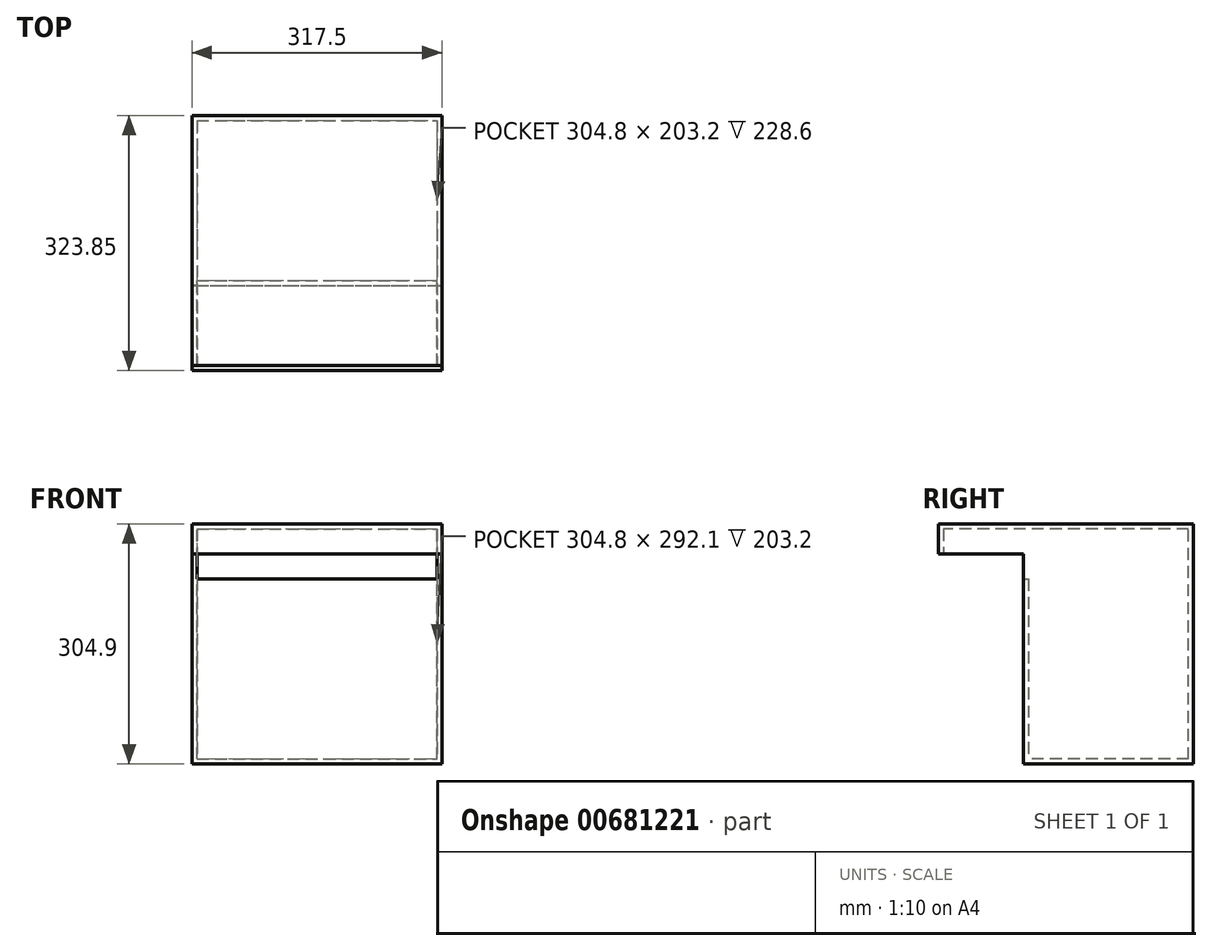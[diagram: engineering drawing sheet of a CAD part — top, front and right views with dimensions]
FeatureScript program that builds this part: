
annotation { "Feature Type Name" : "Feature", "Feature Type Description" : "" }
export const myFeature = defineFeature(function(context is Context, id is Id, definition is map)
    precondition{}
    {
        {
            var Q0;
            Q0=qCreatedBy(makeId("Top.planeOp"),FACE);
            var sketch = newSketch(context, id + "F0", { "sketchPlane" : qUnion([Q0])});
            skLineSegment(sketch, "E0.bottom", {"start": v(0, 0) * mm, "end": v(317.5, 0) * mm});
            skLineSegment(sketch, "E0.top", {"start": v(0, -215.9) * mm, "end": v(317.5, -215.9) * mm});
            skLineSegment(sketch, "E0.left", {"start": v(0, 0) * mm, "end": v(0, -215.9) * mm});
            skLineSegment(sketch, "E0.right", {"start": v(317.5, 0) * mm, "end": v(317.5, -215.9) * mm});
            skSolve(sketch);
        }
        {
            var Q0;
            Q0 = qSketchRegion(id + "F0", true);
            extrude(context, id + "F1", {"entities" : qUnion([Q0]), "oppositeDirection" : true, "depth" : 6.35 * mm, "offsetDistance" : 25.4 * mm});
        }
        {
            var Q0;
            Q0=qCreatedBy(makeId("Front.planeOp"),FACE);
            var sketch = newSketch(context, id + "F2", { "sketchPlane" : qUnion([Q0])});
            skLineSegment(sketch, "E1.bottom", {"start": v(0, 0) * mm, "end": v(317.5, 0) * mm});
            skLineSegment(sketch, "E1.top", {"start": v(0, 292.1) * mm, "end": v(317.5, 292.1) * mm});
            skLineSegment(sketch, "E1.left", {"start": v(0, 0) * mm, "end": v(0, 292.1) * mm});
            skLineSegment(sketch, "E1.right", {"start": v(317.5, 0) * mm, "end": v(317.5, 292.1) * mm});
            skSolve(sketch);
        }
        {
            var Q0;
            Q0=makeQuery(id+"F2.imprint","IMPRINT",FACE,{"disambiguationData":[TD([[makeQuery(id+"F2.imprint","IMPRINT",EDGE,{"derivedFrom":sQuery(id+"F2.wireOp",EDGE,"E1.bottom")}),1.0]])]});
            extrude(context, id + "F3", {"entities" : qUnion([Q0]), "operationType" : NewBodyOperationType.ADD, "depth" : 6.35 * mm, "offsetDistance" : 25.4 * mm});
        }
        {
            var Q0;
            Q0=qCreatedBy(makeId("Right.planeOp"),FACE);
            var sketch = newSketch(context, id + "F4", { "sketchPlane" : qUnion([Q0])});
            skLineSegment(sketch, "E2.bottom", {"start": v(0, 0) * mm, "end": v(-215.9, 0) * mm});
            skLineSegment(sketch, "E2.top", {"start": v(0, 292.1) * mm, "end": v(-215.9, 292.1) * mm});
            skLineSegment(sketch, "E2.left", {"start": v(0, 0) * mm, "end": v(0, 292.1) * mm});
            skLineSegment(sketch, "E2.right", {"start": v(-215.9, 0) * mm, "end": v(-215.9, 292.1) * mm});
            skSolve(sketch);
        }
        {
            var Q0;
            Q0=makeQuery(id+"F4.imprint","IMPRINT",FACE,{"disambiguationData":[TD([[makeQuery(id+"F4.imprint","IMPRINT",EDGE,{"derivedFrom":sQuery(id+"F4.wireOp",EDGE,"E2.bottom")}),-1.0]])]});
            extrude(context, id + "F5", {"entities" : qUnion([Q0]), "operationType" : NewBodyOperationType.ADD, "depth" : 6.35 * mm, "offsetDistance" : 25.4 * mm});
        }
        {
            var Q0;
            Q0=makeQuery(id+"F3.boolean.opBoolean","MERGE",FACE,{"derivedFrom":[makeQuery(id+"F1.opExtrude","SWEPT_FACE",FACE,{"disambiguationData":[OSD([sQuery(id+"F0.wireOp",EDGE,"E0.right")])]}),makeQuery(id+"F3.opExtrude","SWEPT_FACE",FACE,{"disambiguationData":[OSD([sQuery(id+"F2.wireOp",EDGE,"E1.right")])]})]});
            cPlane(context, id + "F6", {"entities" : qUnion([Q0]), "cplaneType" : CPlaneType.OFFSET, "offset" : 0 * mm, "width" : 152.4 * mm, "height" : 152.4 * mm});
        }
        {
            var Q0;
            Q0=qCreatedBy(id+"F6.planeOp",FACE);
            var sketch = newSketch(context, id + "F7", { "sketchPlane" : qUnion([Q0])});
            skLineSegment(sketch, "E3.bottom", {"start": v(0, 292.1) * mm, "end": v(-215.9, 292.1) * mm});
            skLineSegment(sketch, "E3.top", {"start": v(0, 0) * mm, "end": v(-215.9, 0) * mm});
            skLineSegment(sketch, "E3.left", {"start": v(0, 292.1) * mm, "end": v(0, 0) * mm});
            skLineSegment(sketch, "E3.right", {"start": v(-215.9, 292.1) * mm, "end": v(-215.9, 0) * mm});
            skSolve(sketch);
        }
        {
            var Q0;
            Q0 = qSketchRegion(id + "F7", true);
            extrude(context, id + "F8", {"entities" : qUnion([Q0]), "operationType" : NewBodyOperationType.ADD, "oppositeDirection" : true, "depth" : 6.35 * mm, "offsetDistance" : 25.4 * mm});
        }
        {
            var Q0;
            Q0=makeQuery(id+"F8.boolean.opBoolean","MERGE",FACE,{"derivedFrom":[makeQuery(id+"F5.boolean.opBoolean","MERGE",FACE,{"derivedFrom":[makeQuery(id+"F3.opExtrude","SWEPT_FACE",FACE,{"disambiguationData":[OSD([sQuery(id+"F2.wireOp",EDGE,"E1.top")])]}),makeQuery(id+"F5.opExtrude","SWEPT_FACE",FACE,{"disambiguationData":[OSD([sQuery(id+"F4.wireOp",EDGE,"E2.top")])]})]}),makeQuery(id+"F8.opExtrude","SWEPT_FACE",FACE,{"disambiguationData":[OSD([sQuery(id+"F7.wireOp",EDGE,"E3.bottom")])]})]});
            cPlane(context, id + "F9", {"entities" : qUnion([Q0]), "cplaneType" : CPlaneType.OFFSET, "offset" : 0 * mm, "width" : 152.4 * mm, "height" : 152.4 * mm});
        }
        {
            var Q0;
            Q0=qCreatedBy(id+"F9.planeOp",FACE);
            var sketch = newSketch(context, id + "F10", { "sketchPlane" : qUnion([Q0])});
            skLineSegment(sketch, "E4.bottom", {"start": v(0, 0) * mm, "end": v(317.5, 0) * mm});
            skLineSegment(sketch, "E4.top", {"start": v(0, -317.5) * mm, "end": v(317.5, -317.5) * mm});
            skLineSegment(sketch, "E4.left", {"start": v(0, 0) * mm, "end": v(0, -317.5) * mm});
            skLineSegment(sketch, "E4.right", {"start": v(317.5, 0) * mm, "end": v(317.5, -317.5) * mm});
            skSolve(sketch);
        }
        {
            var Q0;
            Q0=makeQuery(id+"F10.imprint","IMPRINT",FACE,{"disambiguationData":[TD([[makeQuery(id+"F10.imprint","IMPRINT",EDGE,{"derivedFrom":sQuery(id+"F10.wireOp",EDGE,"E4.bottom")}),-1.0]])]});
            extrude(context, id + "F11", {"entities" : qUnion([Q0]), "operationType" : NewBodyOperationType.ADD, "depth" : 6.35 * mm, "offsetDistance" : 25.4 * mm});
        }
        {
            var Q0;
            Q0=makeQuery(id+"F11.opExtrude","SWEPT_FACE",FACE,{"disambiguationData":[OSD([sQuery(id+"F10.wireOp",EDGE,"E4.top")])]});
            cPlane(context, id + "F12", {"entities" : qUnion([Q0]), "cplaneType" : CPlaneType.OFFSET, "offset" : 0 * mm, "width" : 152.4 * mm, "height" : 152.4 * mm});
        }
        {
            var Q0;
            Q0=makeQuery(id+"F8.boolean.opBoolean","MERGE",FACE,{"derivedFrom":[makeQuery(id+"F5.boolean.opBoolean","MERGE",FACE,{"derivedFrom":[makeQuery(id+"F1.opExtrude","SWEPT_FACE",FACE,{"disambiguationData":[OSD([sQuery(id+"F0.wireOp",EDGE,"E0.top")])]}),makeQuery(id+"F5.opExtrude","SWEPT_FACE",FACE,{"disambiguationData":[OSD([sQuery(id+"F4.wireOp",EDGE,"E2.right")])]})]}),makeQuery(id+"F8.opExtrude","SWEPT_FACE",FACE,{"disambiguationData":[OSD([sQuery(id+"F7.wireOp",EDGE,"E3.right")])]})]});
            cPlane(context, id + "F13", {"entities" : qUnion([Q0]), "cplaneType" : CPlaneType.OFFSET, "offset" : 0 * mm, "oppositeDirection" : true, "width" : 152.4 * mm, "height" : 152.4 * mm});
        }
        {
            var Q0;
            Q0=qCreatedBy(id+"F13.planeOp",FACE);
            var sketch = newSketch(context, id + "F14", { "sketchPlane" : qUnion([Q0])});
            skLineSegment(sketch, "E5.bottom", {"start": v(0, 228.6) * mm, "end": v(317.5, 228.6) * mm});
            skLineSegment(sketch, "E5.top", {"start": v(0, 0) * mm, "end": v(317.5, 0) * mm});
            skLineSegment(sketch, "E5.left", {"start": v(0, 228.6) * mm, "end": v(0, 0) * mm});
            skLineSegment(sketch, "E5.right", {"start": v(317.5, 228.6) * mm, "end": v(317.5, 0) * mm});
            skSolve(sketch);
        }
        {
            var Q0;
            Q0 = qSketchRegion(id + "F14", true);
            extrude(context, id + "F15", {"entities" : qUnion([Q0]), "operationType" : NewBodyOperationType.ADD, "oppositeDirection" : true, "depth" : 6.35 * mm, "offsetDistance" : 25.4 * mm});
        }
        {
            var Q0;
            Q0=makeQuery(id+"FhI14EcKR7AobF6_1.boolean.opBoolean","MERGE",FACE,{"derivedFrom":[makeQuery(id+"F11.boolean.opBoolean","MERGE",FACE,{"derivedFrom":[makeQuery(id+"F8.boolean.opBoolean","MERGE",FACE,{"derivedFrom":[makeQuery(id+"F3.boolean.opBoolean","MERGE",FACE,{"derivedFrom":[makeQuery(id+"F1.opExtrude","SWEPT_FACE",FACE,{"disambiguationData":[OSD([sQuery(id+"F0.wireOp",EDGE,"E0.right")])]}),makeQuery(id+"F3.opExtrude","SWEPT_FACE",FACE,{"disambiguationData":[OSD([sQuery(id+"F2.wireOp",EDGE,"E1.right")])]})]}),makeQuery(id+"F8.opExtrude","CAP_FACE",FACE,{"disambiguationData":[OSD([sQuery(id+"F7.wireOp",EDGE,"E3.bottom"),sQuery(id+"F7.wireOp",EDGE,"E3.top"),sQuery(id+"F7.wireOp",EDGE,"E3.left"),sQuery(id+"F7.wireOp",EDGE,"E3.right")])],"isStart":true})]}),makeQuery(id+"F11.opExtrude","SWEPT_FACE",FACE,{"disambiguationData":[OSD([sQuery(id+"F10.wireOp",EDGE,"E4.right")])]})]}),makeQuery(id+"FhI14EcKR7AobF6_1.opExtrude","SWEPT_FACE",FACE,{"disambiguationData":[OSD([sQuery(id+"FLD8qPjJOVZHiva_1.wireOp",EDGE,"Go6pk4AO-W8t4-oNwY-yMQV-z4UT52Fjz0Ug.right")])]})]});
            var sketch = newSketch(context, id + "F16", { "sketchPlane" : qUnion([Q0])});
            skLineSegment(sketch, "E6.bottom", {"start": v(-317.5, 298.45) * mm, "end": v(-215.9, 298.45) * mm});
            skLineSegment(sketch, "E6.top", {"start": v(-317.5, 260.35) * mm, "end": v(-215.9, 260.35) * mm});
            skLineSegment(sketch, "E6.left", {"start": v(-317.5, 298.45) * mm, "end": v(-317.5, 260.35) * mm});
            skLineSegment(sketch, "E6.right", {"start": v(-215.9, 298.45) * mm, "end": v(-215.9, 260.35) * mm});
            skSolve(sketch);
        }
        {
            var Q0;
            Q0 = qSketchRegion(id + "F16", true);
            extrude(context, id + "F17", {"entities" : qUnion([Q0]), "operationType" : NewBodyOperationType.ADD, "oppositeDirection" : true, "depth" : 6.35 * mm, "offsetDistance" : 25.4 * mm});
        }
        {
            var Q0;
            Q0=makeQuery(id+"FhI14EcKR7AobF6_1.boolean.opBoolean","MERGE",FACE,{"derivedFrom":[makeQuery(id+"F11.boolean.opBoolean","MERGE",FACE,{"derivedFrom":[makeQuery(id+"F5.boolean.opBoolean","MERGE",FACE,{"derivedFrom":[makeQuery(id+"F3.boolean.opBoolean","MERGE",FACE,{"derivedFrom":[makeQuery(id+"F1.opExtrude","SWEPT_FACE",FACE,{"disambiguationData":[OSD([sQuery(id+"F0.wireOp",EDGE,"E0.left")])]}),makeQuery(id+"F3.opExtrude","SWEPT_FACE",FACE,{"disambiguationData":[OSD([sQuery(id+"F2.wireOp",EDGE,"E1.left")])]})]}),makeQuery(id+"F5.opExtrude","CAP_FACE",FACE,{"disambiguationData":[OSD([sQuery(id+"F4.wireOp",EDGE,"E2.bottom"),sQuery(id+"F4.wireOp",EDGE,"E2.top"),sQuery(id+"F4.wireOp",EDGE,"E2.left"),sQuery(id+"F4.wireOp",EDGE,"E2.right")])],"isStart":true})]}),makeQuery(id+"F11.opExtrude","SWEPT_FACE",FACE,{"disambiguationData":[OSD([sQuery(id+"F10.wireOp",EDGE,"E4.left")])]})]}),makeQuery(id+"FhI14EcKR7AobF6_1.opExtrude","SWEPT_FACE",FACE,{"disambiguationData":[OSD([sQuery(id+"FLD8qPjJOVZHiva_1.wireOp",EDGE,"Go6pk4AO-W8t4-oNwY-yMQV-z4UT52Fjz0Ug.left")])]})]});
            var sketch = newSketch(context, id + "F18", { "sketchPlane" : qUnion([Q0])});
            skLineSegment(sketch, "E7.bottom", {"start": v(317.5, 298.45) * mm, "end": v(215.9, 298.45) * mm});
            skLineSegment(sketch, "E7.top", {"start": v(317.5, 260.35) * mm, "end": v(215.9, 260.35) * mm});
            skLineSegment(sketch, "E7.left", {"start": v(317.5, 298.45) * mm, "end": v(317.5, 260.35) * mm});
            skLineSegment(sketch, "E7.right", {"start": v(215.9, 298.45) * mm, "end": v(215.9, 260.35) * mm});
            skSolve(sketch);
        }
        {
            var Q0;
            Q0 = qSketchRegion(id + "F18", true);
            extrude(context, id + "F19", {"entities" : qUnion([Q0]), "operationType" : NewBodyOperationType.ADD, "oppositeDirection" : true, "depth" : 6.35 * mm, "offsetDistance" : 25.4 * mm});
        }
        {
            var Q0;
            Q0=qCreatedBy(id+"F12.planeOp",FACE);
            var sketch = newSketch(context, id + "F20", { "sketchPlane" : qUnion([Q0])});
            skLineSegment(sketch, "E8.bottom", {"start": v(0, 298.55) * mm, "end": v(317.5, 298.55) * mm});
            skLineSegment(sketch, "E8.top", {"start": v(0, 260.45) * mm, "end": v(317.5, 260.45) * mm});
            skLineSegment(sketch, "E8.left", {"start": v(0, 298.55) * mm, "end": v(0, 260.45) * mm});
            skLineSegment(sketch, "E8.right", {"start": v(317.5, 298.55) * mm, "end": v(317.5, 260.45) * mm});
            skSolve(sketch);
        }
        {
            var Q0;
            Q0 = qSketchRegion(id + "F20", true);
            extrude(context, id + "F21", {"entities" : qUnion([Q0]), "operationType" : NewBodyOperationType.ADD, "depth" : 6.35 * mm, "offsetDistance" : 25.4 * mm});
        }
    });
